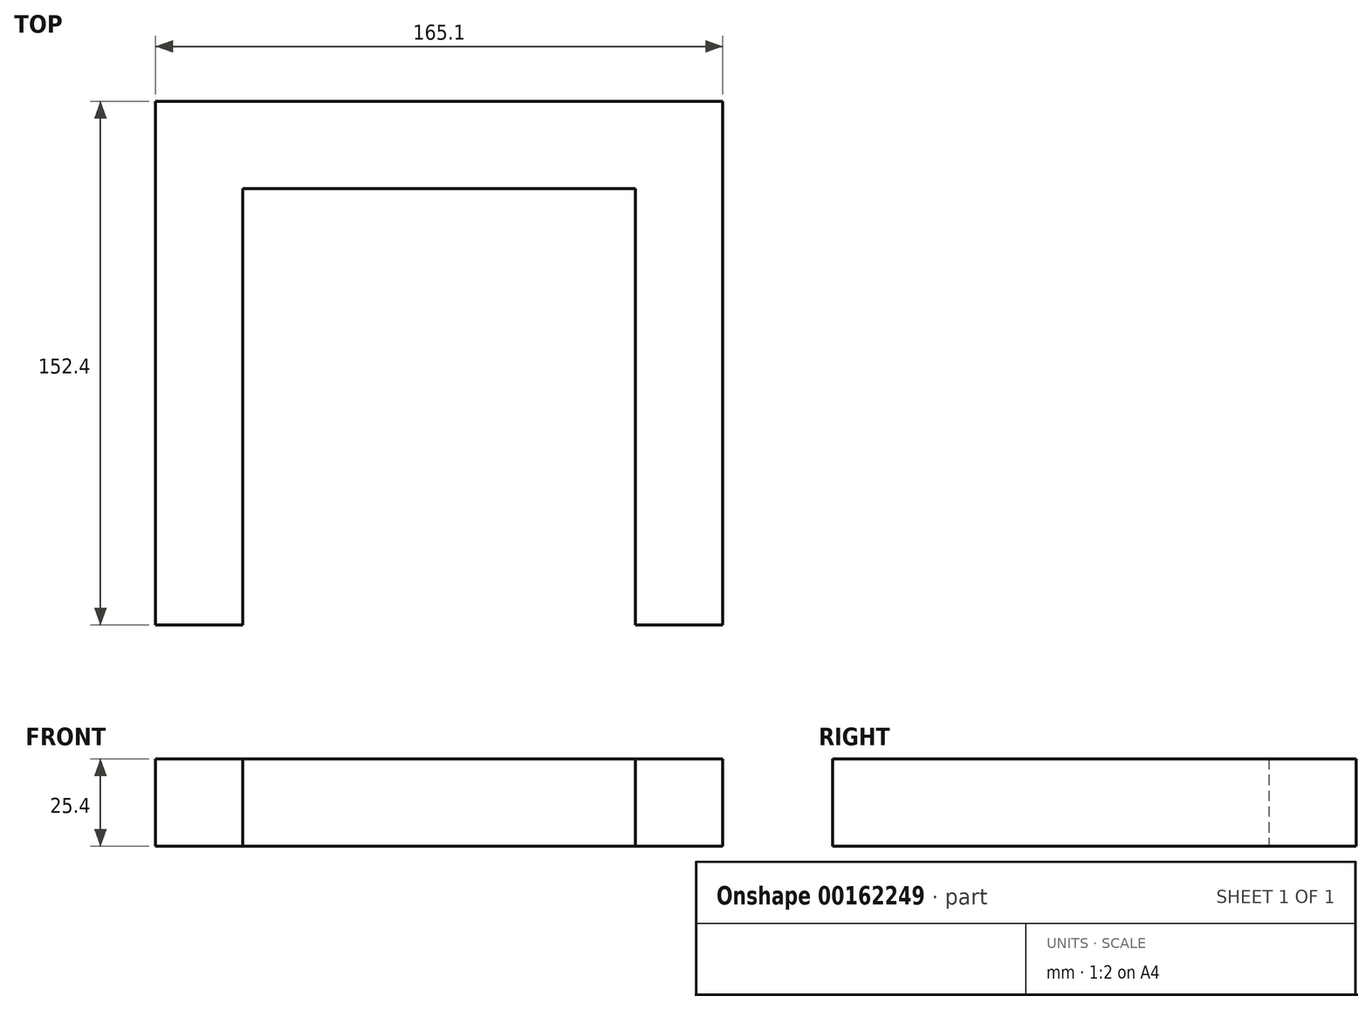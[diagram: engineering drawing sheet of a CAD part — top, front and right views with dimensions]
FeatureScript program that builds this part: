
annotation { "Feature Type Name" : "Feature", "Feature Type Description" : "" }
export const myFeature = defineFeature(function(context is Context, id is Id, definition is map)
    precondition{}
    {
        {
            var Q0;
            Q0=qCreatedBy(makeId("Front.planeOp"),FACE);
            var sketch = newSketch(context, id + "F0", { "sketchPlane" : qUnion([Q0])});
            skLineSegment(sketch, "E0.bottom", {"start": v(82.55, -12.7) * mm, "end": v(-82.55, -12.7) * mm});
            skLineSegment(sketch, "E0.top", {"start": v(82.55, 12.7) * mm, "end": v(-82.55, 12.7) * mm});
            skLineSegment(sketch, "E0.left", {"start": v(82.55, -12.7) * mm, "end": v(82.55, 12.7) * mm});
            skLineSegment(sketch, "E0.right", {"start": v(-82.55, -12.7) * mm, "end": v(-82.55, 12.7) * mm});
            skPoint(sketch, "E0.middle", {"position": v(0, 0) * mm});
            skSolve(sketch);
        }
        {
            var Q0;
            Q0=makeQuery(id+"F0.imprint","IMPRINT",FACE,{"disambiguationData":[TD([[makeQuery(id+"F0.imprint","IMPRINT",EDGE,{"derivedFrom":sQuery(id+"F0.wireOp",EDGE,"E0.bottom")}),-1.0]])]});
            extrude(context, id + "F1", {"entities" : qUnion([Q0]), "depth" : 25.4 * mm});
        }
        {
            var Q0;
            Q0=makeQuery(id+"F1.opExtrude","CAP_FACE",FACE,{"disambiguationData":[OSD([sQuery(id+"F0.wireOp",EDGE,"E0.bottom"),sQuery(id+"F0.wireOp",EDGE,"E0.top"),sQuery(id+"F0.wireOp",EDGE,"E0.left"),sQuery(id+"F0.wireOp",EDGE,"E0.right")])],"isStart":false});
            var sketch = newSketch(context, id + "F2", { "sketchPlane" : qUnion([Q0])});
            skLineSegment(sketch, "E1.bottom", {"start": v(-82.55, 12.7) * mm, "end": v(-57.15, 12.7) * mm});
            skLineSegment(sketch, "E1.top", {"start": v(-82.55, -12.7) * mm, "end": v(-57.15, -12.7) * mm});
            skLineSegment(sketch, "E1.left", {"start": v(-82.55, 12.7) * mm, "end": v(-82.55, -12.7) * mm});
            skLineSegment(sketch, "E1.right", {"start": v(-57.15, 12.7) * mm, "end": v(-57.15, -12.7) * mm});
            skLineSegment(sketch, "E2.bottom", {"start": v(82.55, 12.7) * mm, "end": v(57.15, 12.7) * mm});
            skLineSegment(sketch, "E2.top", {"start": v(82.55, -12.7) * mm, "end": v(57.15, -12.7) * mm});
            skLineSegment(sketch, "E2.left", {"start": v(82.55, 12.7) * mm, "end": v(82.55, -12.7) * mm});
            skLineSegment(sketch, "E2.right", {"start": v(57.15, 12.7) * mm, "end": v(57.15, -12.7) * mm});
            skSolve(sketch);
        }
        {
            var Q0;
            Q0=makeQuery(id+"F2.imprint","IMPRINT",FACE,{"disambiguationData":[TD([[makeQuery(id+"F2.imprint","IMPRINT",EDGE,{"derivedFrom":sQuery(id+"F2.wireOp",EDGE,"E1.bottom")}),1.0]])]});
            var Q1;
            Q1=makeQuery(id+"F2.imprint","IMPRINT",FACE,{"disambiguationData":[TD([[makeQuery(id+"F2.imprint","IMPRINT",EDGE,{"derivedFrom":sQuery(id+"F2.wireOp",EDGE,"E2.bottom")}),1.0]])]});
            extrude(context, id + "F3", {"entities" : qUnion([Q0, Q1]), "operationType" : NewBodyOperationType.ADD, "depth" : 127 * mm});
        }
    });
